# Revit family: HeartFelt-Linear-Luxalon Suspension Adjust. Spring_HunterDouglasEurope.LOG200
name_source: partatom
category: Specialty Equipment
revit_build: Autodesk Revit 2016 (Build: 20150220_1215(x64)
units: mm (PartAtom-declared; Revit-internal decimal feet)

## family parameters
Always vertical = No
Cut with Voids When Loaded = No
OmniClass Number = 23.35.70.24.11.11.11
OmniClass Title = Suspended Ceilings, Suspension Assembly
Part Type = Normal
Room Calculation Point = No
Round Connector Dimension = Use Diameter
Shared = No
Work Plane-Based = No

## types (1)
- Luxalon Suspension Adjustment Spring
    Alloy = EN 10132 CK60 H+A
    Article Code = 33.4795
    EN13501-1_Fire rating = Class A1
    Manufacturer = Hunter Douglas
    Material = Galvanized Steel_HunterDouglasEurope
    Model = Luxalon Suspension Adjustment Spring
    Product Data = http://assets2.hunterdouglascontract.com
    Product Line = HeartFelt® Linear
    Subcategory = HeartFelt® Ceilings
    Thickness = 0.5 mm  [stored 0.00164042 ft]
    URL = http://www.hunterdouglasarchitectural.eu

note: [stored X ft] marks values corroborated as IEEE doubles in the binary element streams (Revit-internal decimal feet)

## geometry (parser evidence)
native form markers: Sweep x2
no freeform markers — native parametric forms only
